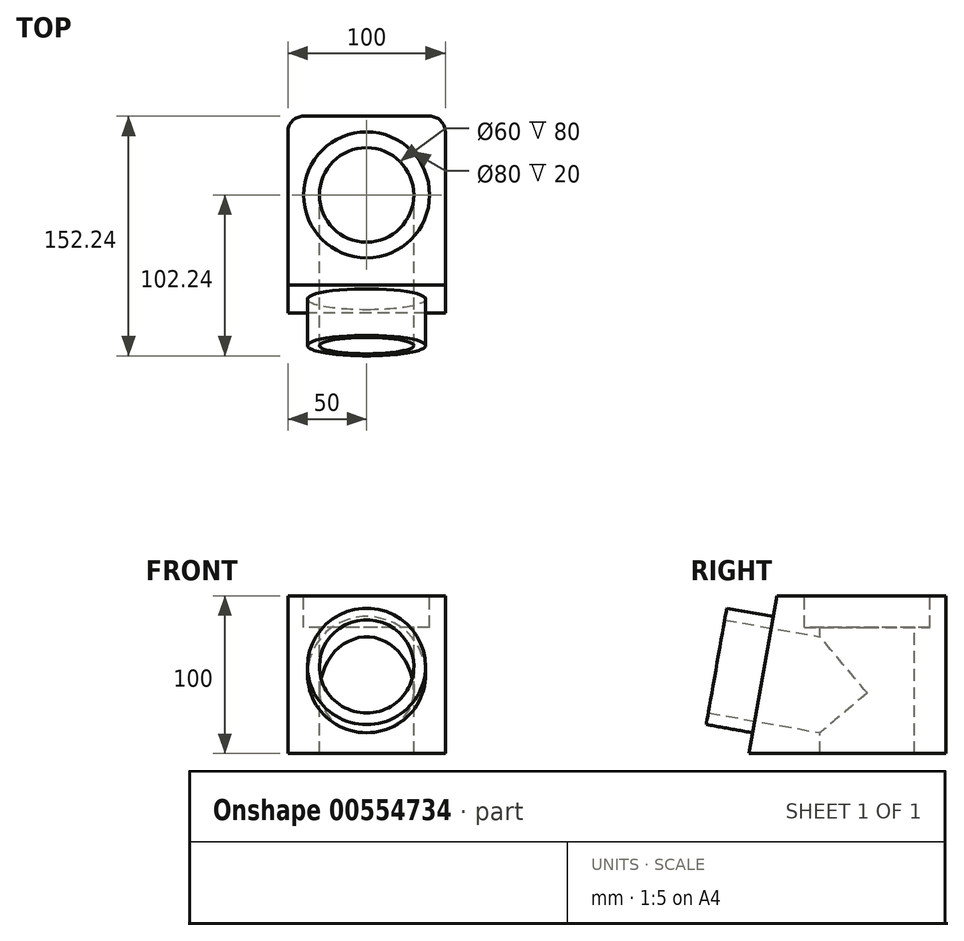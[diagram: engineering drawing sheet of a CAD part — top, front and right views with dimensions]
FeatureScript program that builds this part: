
annotation { "Feature Type Name" : "Feature", "Feature Type Description" : "" }
export const myFeature = defineFeature(function(context is Context, id is Id, definition is map)
    precondition{}
    {
        {
            var Q0;
            Q0=qCreatedBy(makeId("Top.planeOp"),FACE);
            var sketch = newSketch(context, id + "F0", { "sketchPlane" : qUnion([Q0])});
            skLineSegment(sketch, "E0.bottom", {"start": v(-50, -50) * mm, "end": v(50, -50) * mm});
            skLineSegment(sketch, "E0.top", {"start": v(-50, 50) * mm, "end": v(50, 50) * mm});
            skLineSegment(sketch, "E0.left", {"start": v(-50, -50) * mm, "end": v(-50, 50) * mm});
            skLineSegment(sketch, "E0.right", {"start": v(50, -50) * mm, "end": v(50, 50) * mm});
            skPoint(sketch, "E0.middle", {"position": v(0, 0) * mm});
            skSolve(sketch);
        }
        {
            var Q0;
            Q0=makeQuery(id+"F0.imprint","IMPRINT",FACE,{"disambiguationData":[TD([[makeQuery(id+"F0.imprint","IMPRINT",EDGE,{"derivedFrom":sQuery(id+"F0.wireOp",EDGE,"E0.bottom")}),1.0]])]});
            extrude(context, id + "F1", {"entities" : qUnion([Q0]), "endBound" : BoundingType.SYMMETRIC, "depth" : 100 * mm, "offsetDistance" : 25 * mm});
        }
        {
            var Q0;
            Q0=makeQuery(id+"F1.opExtrude","CAP_FACE",FACE,{"disambiguationData":[OSD([sQuery(id+"F0.wireOp",EDGE,"E0.bottom"),sQuery(id+"F0.wireOp",EDGE,"E0.top"),sQuery(id+"F0.wireOp",EDGE,"E0.left"),sQuery(id+"F0.wireOp",EDGE,"E0.right")])],"isStart":false});
            var sketch = newSketch(context, id + "F2", { "sketchPlane" : qUnion([Q0])});
            skCircle(sketch, "E1", {"center": v(0, 0) * mm, "radius": 40 * mm});
            skCircle(sketch, "E2", {"center": v(0, 0) * mm, "radius": 30 * mm});
            skSolve(sketch);
        }
        {
            var Q0;
            Q0=makeQuery(id+"F2.imprint","IMPRINT",FACE,{"disambiguationData":[TD([[makeQuery(id+"F2.imprint","IMPRINT",EDGE,{"derivedFrom":sQuery(id+"F2.wireOp",EDGE,"E2")}),1.0]])]});
            extrude(context, id + "F3", {"entities" : qUnion([Q0]), "operationType" : NewBodyOperationType.REMOVE, "endBound" : BoundingType.THROUGH_ALL, "oppositeDirection" : true, "depth" : 25 * mm, "offsetDistance" : 25 * mm});
        }
        {
            var Q0;
            Q0 = qSketchRegion(id + "F2", true);
            extrude(context, id + "F4", {"entities" : qUnion([Q0]), "operationType" : NewBodyOperationType.REMOVE, "oppositeDirection" : true, "depth" : 20 * mm, "offsetDistance" : 25 * mm});
        }
        {
            var Q0;
            Q0=makeQuery(id+"F1.opExtrude","SWEPT_FACE",FACE,{"disambiguationData":[OSD([sQuery(id+"F0.wireOp",EDGE,"E0.left")])]});
            var sketch = newSketch(context, id + "F5", { "sketchPlane" : qUnion([Q0])});
            skLineSegment(sketch, "E3", {"start": v(50, -50) * mm, "end": v(75, -50) * mm});
            skLineSegment(sketch, "E4", {"start": v(75, -50) * mm, "end": v(57.37, 50) * mm});
            skLineSegment(sketch, "E5", {"start": v(57.37, 50) * mm, "end": v(50, 50) * mm});
            skLineSegment(sketch, "E6", {"start": v(50, 50) * mm, "end": v(50, -50) * mm});
            skSolve(sketch);
        }
        {
            var Q0;
            Q0=makeQuery(id+"F5.imprint","IMPRINT",FACE,{"disambiguationData":[TD([[makeQuery(id+"F5.imprint","IMPRINT",EDGE,{"derivedFrom":sQuery(id+"F5.wireOp",EDGE,"E3")}),1.0]])]});
            var Q1;
            Q1=makeQuery(id+"F1.opExtrude","SWEPT_FACE",FACE,{"disambiguationData":[OSD([sQuery(id+"F0.wireOp",EDGE,"E0.right")])]});
            extrude(context, id + "F6", {"entities" : qUnion([Q0]), "operationType" : NewBodyOperationType.ADD, "endBound" : BoundingType.UP_TO_SURFACE, "oppositeDirection" : true, "depth" : 25 * mm, "endBoundEntityFace" : qUnion([Q1]), "offsetDistance" : 25 * mm});
        }
        {
            var Q0;
            Q0=makeQuery(id+"F6.opExtrude","SWEPT_FACE",FACE,{"disambiguationData":[OSD([sQuery(id+"F5.wireOp",EDGE,"E4")])]});
            var sketch = newSketch(context, id + "F7", { "sketchPlane" : qUnion([Q0])});
            skCircle(sketch, "E7", {"center": v(0, -11.5) * mm, "radius": 37.5 * mm});
            skLineSegment(sketch, "E8", {"start": v(-50, -62.26) * mm, "end": v(50, 39.28) * mm, "construction": true});
            skLineSegment(sketch, "E9", {"start": v(-50, 39.28) * mm, "end": v(50, -62.26) * mm, "construction": true});
            skCircle(sketch, "E10", {"center": v(0, -11.5) * mm, "radius": 30 * mm});
            skSolve(sketch);
        }
        {
            var Q0;
            Q0=makeQuery(id+"F7.imprint","IMPRINT",FACE,{"disambiguationData":[TD([[makeQuery(id+"F7.imprint","IMPRINT",EDGE,{"derivedFrom":sQuery(id+"F7.wireOp",EDGE,"E7")}),1.0]])]});
            extrude(context, id + "F8", {"entities" : qUnion([Q0]), "operationType" : NewBodyOperationType.ADD, "depth" : 30 * mm, "offsetDistance" : 25 * mm});
        }
        {
            var Q0;
            Q0=makeQuery(id+"F8.boolean.opBoolean","SPLIT",FACE,{"disambiguationData":[TD([makeQuery(id+"F8.opExtrude","SWEPT_FACE",FACE,{"disambiguationData":[OSD([sQuery(id+"F7.wireOp",EDGE,"E10")])]})])],"derivedFrom":makeQuery(id+"F6.opExtrude","SWEPT_FACE",FACE,{"disambiguationData":[OSD([sQuery(id+"F5.wireOp",EDGE,"E4")])]})});
            extrude(context, id + "F9", {"entities" : qUnion([Q0]), "operationType" : NewBodyOperationType.REMOVE, "endBound" : BoundingType.UP_TO_NEXT, "oppositeDirection" : true, "depth" : 25 * mm, "offsetDistance" : 25 * mm});
        }
        {
            var Q0;
            Q0=makeQuery(id+"F1.opExtrude","SWEPT_EDGE",EDGE,{"disambiguationData":[OSD([sQuery(id+"F0.wireOp",EDGE,"E0.top"),sQuery(id+"F0.wireOp",EDGE,"E0.right")])]});
            var Q1;
            Q1=makeQuery(id+"F1.opExtrude","SWEPT_EDGE",EDGE,{"disambiguationData":[OSD([sQuery(id+"F0.wireOp",EDGE,"E0.top"),sQuery(id+"F0.wireOp",EDGE,"E0.left")])]});
            fillet(context, id + "F10", {"entities" : qUnion([Q0, Q1]), "radius" : 10 * mm, "tangentPropagation" : true, "allowEdgeOverflow" : false});
        }
    });
